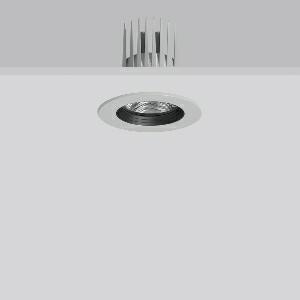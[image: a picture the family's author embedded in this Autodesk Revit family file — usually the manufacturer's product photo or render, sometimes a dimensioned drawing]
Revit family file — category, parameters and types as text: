
# Revit family: heledon_mini_e_901748_004_76_ff59
name_source: partatom
category: Lighting Fixtures
units: mm (PartAtom-declared; Revit-internal decimal feet)

## family parameters
Cut with Voids When Loaded = No
Host = Face
Light Source = No
Part Type = Normal
Room Calculation Point = No
Round Connector Dimension = Use Diameter
Shared = No

## types (1)
- HELEDON mini E (1 x LED Modul 930, 3550 lm, 3000)
    Apparent Load = 29 VA
    Approval mark = CE
    CIE Flux Codes = 100 100 100 100 100
    Color Rendering = 90
    Color Temperature = 3000
    Default Elevation = 1800 mm
    Description = Series: HELEDON mini
Round recessed downlight. Housing: die-cast aluminium, powder-coated. Black plastic ring and recessed LED to prevent glare from the side. Optical assembly with reflector made of MIRO-Silver with 98% total light reflection for outstanding efficiency - can be changed without tools. Best colour rendering index Ra>90. Suitable for Recessed ceiling mounting. Installation without tools thanks to spring fastening system. Including separate LED converter with connecting cable 600 mm.High quality converter without flickering and stroboscopic effect. Through-wiring box (5 pole) available as accessory. The following accessories can be mounted without use of tools: interchangeable lenses, decorative glasses, honeycomb louvre, clear and frosted diffusers, white interchangeable plastic ring. 
Colour: silver
Diameter: 124 mm
Height: 3 mm
Cut-out diameter: 114 mm
Recess height: 170 mm
Luminaire: recess height: 120 mm
Lamp: LED
Socket: without socket
Colour temperature: 3000K
Colour rendering index (CRI): 92
System power: 29 W
Rated luminous flux: 3550 lm
Luminous efficiency: 122 lm/W
Control gear: Converter, dimmable, DALI
Protection class: II
Type of protection: IP 20
    Height = 0 mm  [stored 0 ft]
    Lamp = 1 x LED Modul 930
    Lamp Light Flux = 3550 lm
    Lamp count = 1
    Length = 124 mm  [stored 0.406824 ft]
    Lifetime = 50000 h
    Luminous efficacy = 122 lm/W
    Manufacturer = RZB
    ModVariant = No
    Model = 901748.004.76
    Mounting Place = Ceiling
    Mounting Type = Recessed
    Number of Poles = 1
    OnlyDefault = Yes
    Power Factor = 1
    Product Name = HELEDON mini E
    Product group = Recessed downlights
    ProductGroupID = 402
    Protection Class = Protection class II
    Protection Degree = IP 20
    RLX_Detail_Level = 1
    RLX_Emergency_Light_Flux = 0 lm
    RLX_Emergency_Type = 0
    RLX_Emergency_Type_DB = No
    RlxData = <blob elided: 128197 chars, md5=5fac8882>
    Socket = socket
    Standby Power = 0 W
    System Light Flux = 3550 lm
    System Power = 29 W
    Type Comments = Product without accessories
    Type Image = 901657.004.jpg
    URL = http://relux.com
    VarID = ---
    Voltage = 230 V
    Voltage Range = 220-240 V
    Weight = 0.00 kg
    Width = 0 mm  [stored 0 ft]

note: [stored X ft] marks values corroborated as IEEE doubles in the binary element streams (Revit-internal decimal feet)

## geometry (parser evidence)
native form markers: Blend x4, Sweep x11
no freeform markers — native parametric forms only
